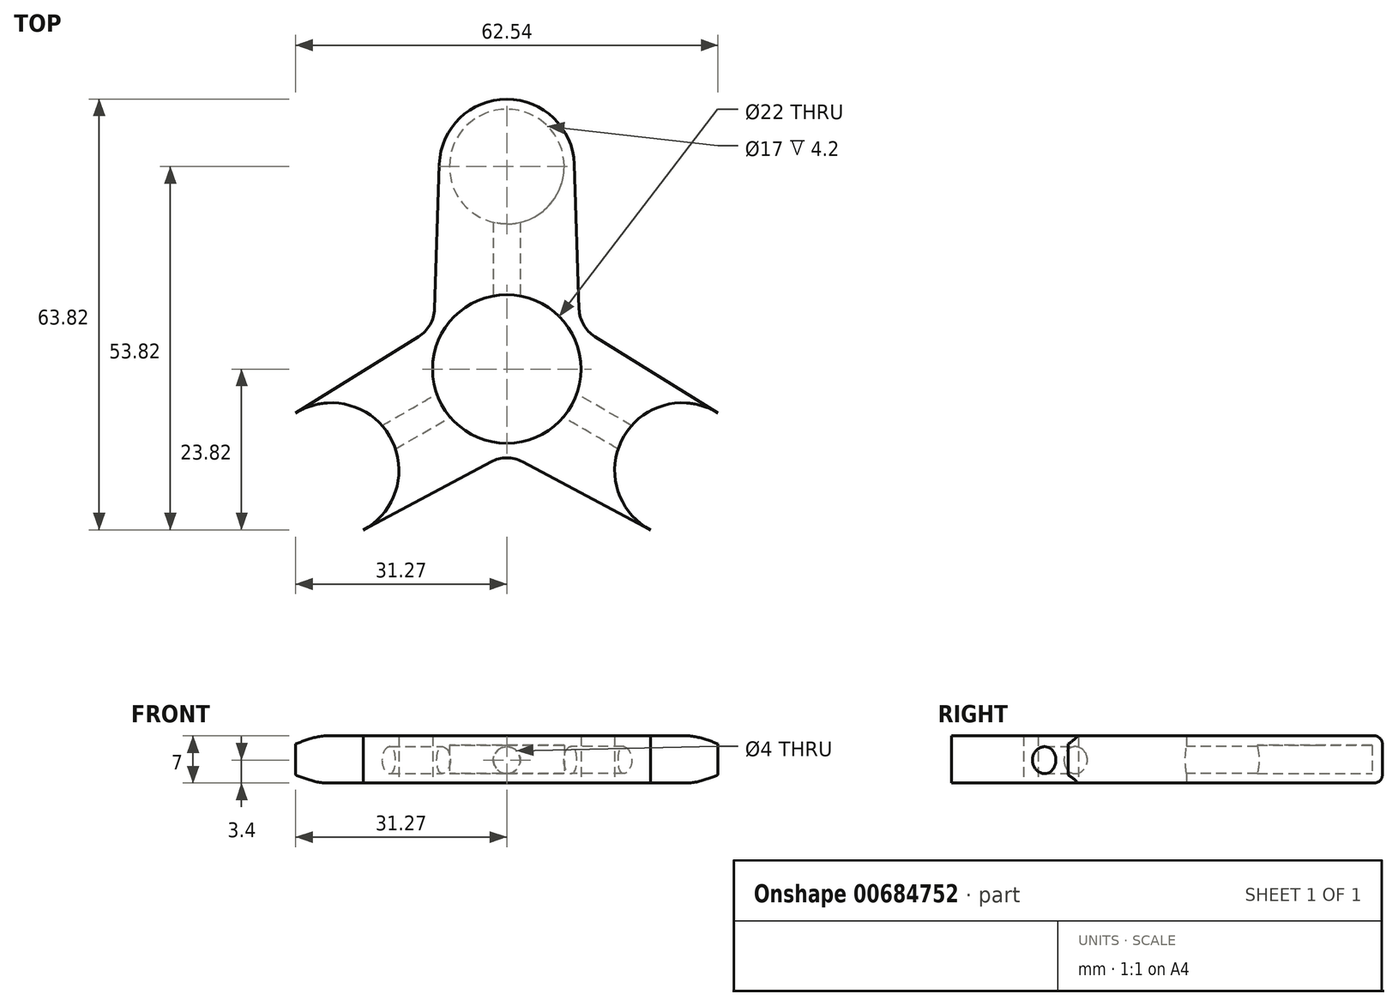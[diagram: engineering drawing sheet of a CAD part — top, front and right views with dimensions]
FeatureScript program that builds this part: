
annotation { "Feature Type Name" : "Feature", "Feature Type Description" : "" }
export const myFeature = defineFeature(function(context is Context, id is Id, definition is map)
    precondition{}
    {
        {
            var Q0;
            Q0=qCreatedBy(makeId("Top.planeOp"),FACE);
            var sketch = newSketch(context, id + "F0", { "sketchPlane" : qUnion([Q0])});
            skCircle(sketch, "E0", {"center": v(0, 0) * mm, "radius": 11 * mm});
            skLineSegment(sketch, "E1", {"start": v(-51.96, 30) * mm, "end": v(51.96, -30) * mm, "construction": true});
            skLineSegment(sketch, "E2.MirrorCS", {"start": v(51.96, 30) * mm, "end": v(-51.96, -30) * mm, "construction": true});
            skCircle(sketch, "E3", {"center": v(0, 30) * mm, "radius": 10 * mm});
            skCircle(sketch, "E4.MirrorC", {"center": v(-25.98, -15) * mm, "radius": 10 * mm});
            skCircle(sketch, "E5.MirrorC", {"center": v(25.98, -15) * mm, "radius": 10 * mm});
            skLineSegment(sketch, "E6", {"start": v(-10, 30.33) * mm, "end": v(-10.7, 8.9) * mm});
            skLineSegment(sketch, "E7", {"start": v(-13.06, 4.82) * mm, "end": v(-31.27, -6.51) * mm});
            skLineSegment(sketch, "E8", {"start": v(10, 30.33) * mm, "end": v(10.7, 8.9) * mm});
            skLineSegment(sketch, "E9.MirrorCS", {"start": v(-21.27, -23.82) * mm, "end": v(-2.35, -13.73) * mm});
            skLineSegment(sketch, "E10.MirrorCS", {"start": v(21.27, -23.82) * mm, "end": v(2.35, -13.73) * mm});
            skLineSegment(sketch, "E11.MirrorCS", {"start": v(31.27, -6.51) * mm, "end": v(13.06, 4.82) * mm});
            skPoint(sketch, "E12.newPointA", {"position": v(-11, 0) * mm});
            skArc(sketch, "E12.filletArc", {"start": v(-13.06, 4.82) * mm, "mid": v(-11.38, 6.57) * mm, "end": v(-10.7, 8.9) * mm});
            skPoint(sketch, "E13.newPointA", {"position": v(5.5, 9.53) * mm});
            skPoint(sketch, "E13.newPointB", {"position": v(11, 0) * mm});
            skArc(sketch, "E13.filletArc", {"start": v(10.7, 8.9) * mm, "mid": v(11.38, 6.57) * mm, "end": v(13.06, 4.82) * mm});
            skPoint(sketch, "E14.newPointA", {"position": v(5.5, -9.53) * mm});
            skPoint(sketch, "E14.newPointB", {"position": v(-5.5, -9.53) * mm});
            skArc(sketch, "E14.filletArc", {"start": v(2.35, -13.73) * mm, "mid": v(0, -13.14) * mm, "end": v(-2.35, -13.73) * mm});
            skLineSegment(sketch, "E15", {"start": v(-8.84, -35.83) * mm, "end": v(22.73, 18.85) * mm, "construction": true});
            skLineSegment(sketch, "E16.MirrorCS", {"start": v(8.84, -35.83) * mm, "end": v(-22.73, 18.85) * mm, "construction": true});
            skSolve(sketch);
        }
        {
            var Q0;
            Q0=makeQuery(id+"F0.imprint","IMPRINT",FACE,{"disambiguationData":[TD([[makeQuery(id+"F0.imprint","IMPRINT",EDGE,{"derivedFrom":sQuery(id+"F0.wireOp",EDGE,"E0")}),-1.0]])]});
            var Q1;
            {var subQ0=sQuery(id+"F0.wireOp",EDGE,"E3");var subQ1=makeQuery(id+"F0.imprint","INTERSECT",VERTEX,{"derivedFrom":[subQ0,sQuery(id+"F0.wireOp",EDGE,"E8")]});Q1=makeQuery(id+"F0.imprint","IMPRINT",FACE,{"disambiguationData":[TD([[makeQuery(id+"F0.imprint","IMPRINT",EDGE,{"disambiguationData":[TD([[subQ1,-1.0]])],"derivedFrom":subQ0}),1.0]])]});}
            var Q2;
            {var subQ0=sQuery(id+"F0.wireOp",EDGE,"E4.MirrorC");var subQ1=makeQuery(id+"F0.imprint","INTERSECT",VERTEX,{"derivedFrom":[subQ0,sQuery(id+"F0.wireOp",EDGE,"E7")]});Q2=makeQuery(id+"F0.imprint","IMPRINT",FACE,{"disambiguationData":[TD([[makeQuery(id+"F0.imprint","IMPRINT",EDGE,{"disambiguationData":[TD([[subQ1,1.0]])],"derivedFrom":subQ0}),-1.0]])]});}
            var Q3;
            {var subQ0=sQuery(id+"F0.wireOp",EDGE,"E5.MirrorC");var subQ1=makeQuery(id+"F0.imprint","INTERSECT",VERTEX,{"derivedFrom":[subQ0,sQuery(id+"F0.wireOp",EDGE,"E11.MirrorCS")]});Q3=makeQuery(id+"F0.imprint","IMPRINT",FACE,{"disambiguationData":[TD([[makeQuery(id+"F0.imprint","IMPRINT",EDGE,{"disambiguationData":[TD([[subQ1,-1.0]])],"derivedFrom":subQ0}),-1.0]])]});}
            var Q4;
            {var subQ5=sQuery(id+"F0.wireOp",EDGE,"lwHCKfIK-zS6e-CTAC-9HsI-oUIeT1y9pyuL");Q4=makeQuery(id+"F0.imprint","IMPRINT",FACE,{"disambiguationData":[TD([[makeQuery(id+"F0.imprint","IMPRINT",EDGE,{"derivedFrom":subQ5}),1.0]])]});}
            var Q5;
            {var subQ1=sQuery(id+"F0.wireOp",EDGE,"E8");Q5=makeQuery(id+"F0.imprint","IMPRINT",FACE,{"disambiguationData":[TD([[makeQuery(id+"F0.imprint","IMPRINT",EDGE,{"derivedFrom":subQ1}),1.0]])]});}
            extrude(context, id + "F1", {"entities" : qUnion([Q0, Q1, Q2, Q3, Q4, Q5]), "depth" : 7 * mm, "offsetDistance" : 25 * mm});
        }
        {
            var Q0;
            Q0=qCreatedBy(makeId("Top.planeOp"),FACE);
            cPlane(context, id + "F2", {"entities" : qUnion([Q0]), "cplaneType" : CPlaneType.OFFSET, "offset" : 1.4 * mm, "width" : 150 * mm, "height" : 150 * mm});
        }
        {
            var Q0;
            Q0=qCreatedBy(id+"F2.planeOp",FACE);
            var sketch = newSketch(context, id + "F3", { "sketchPlane" : qUnion([Q0])});
            skPoint(sketch, "E17.0", {"position": v(0, 30) * mm});
            skPoint(sketch, "E18.0", {"position": v(25.98, -15) * mm});
            skPoint(sketch, "E19.0", {"position": v(-25.98, -15) * mm});
            skCircle(sketch, "E20", {"center": v(25.98, -15) * mm, "radius": 8.5 * mm});
            skCircle(sketch, "E21", {"center": v(-25.98, -15) * mm, "radius": 8.5 * mm});
            skCircle(sketch, "E22", {"center": v(0, 30) * mm, "radius": 8.5 * mm});
            skSolve(sketch);
        }
        {
            var Q0;
            Q0=qSketchRegion(id+"F3",true);
            extrude(context, id + "F4", {"entities" : qUnion([Q0]), "operationType" : NewBodyOperationType.REMOVE, "depth" : 4.2 * mm, "offsetDistance" : 25 * mm});
        }
        {
            var Q0;
            Q0=qCreatedBy(makeId("Front.planeOp"),FACE);
            cPlane(context, id + "F5", {"entities" : qUnion([Q0]), "cplaneType" : CPlaneType.OFFSET, "offset" : 10 * mm, "oppositeDirection" : true, "width" : 150 * mm, "height" : 150 * mm});
        }
        {
            var Q0;
            Q0=qCreatedBy(id+"F5.planeOp",FACE);
            var sketch = newSketch(context, id + "F6", { "sketchPlane" : qUnion([Q0])});
            skCircle(sketch, "E23", {"center": v(0, 3.4) * mm, "radius": 2 * mm});
            skSolve(sketch);
        }
        {
            var Q0;
            Q0=makeQuery(id+"F6.imprint","IMPRINT",FACE,{"disambiguationData":[TD([[makeQuery(id+"F6.imprint","IMPRINT",EDGE,{"derivedFrom":sQuery(id+"F6.wireOp",EDGE,"E23")}),1.0]])]});
            extrude(context, id + "F7", {"entities" : qUnion([Q0]), "operationType" : NewBodyOperationType.REMOVE, "oppositeDirection" : true, "depth" : 12 * mm, "offsetDistance" : 25 * mm});
        }
        {
            var Q0;
            Q0=sQuery(id+"F0.wireOp",EDGE,"E15");
            cPlane(context, id + "F8", {"entities" : qUnion([Q0]), "cplaneType" : CPlaneType.LINE_ANGLE, "offset" : 25 * mm, "angle" : 90 * degree, "width" : 150 * mm, "height" : 150 * mm});
        }
        {
            var Q0;
            Q0=qCreatedBy(id+"F8.planeOp",FACE);
            var sketch = newSketch(context, id + "F9", { "sketchPlane" : qUnion([Q0])});
            skCircle(sketch, "E24", {"center": v(0, 3.4) * mm, "radius": 2 * mm});
            skSolve(sketch);
        }
        {
            var Q0;
            Q0=makeQuery(id+"F9.imprint","IMPRINT",FACE,{"disambiguationData":[TD([[makeQuery(id+"F9.imprint","IMPRINT",EDGE,{"derivedFrom":sQuery(id+"F9.wireOp",EDGE,"E24")}),1.0]])]});
            extrude(context, id + "F10", {"entities" : qUnion([Q0]), "operationType" : NewBodyOperationType.REMOVE, "depth" : 12 * mm, "offsetDistance" : 25 * mm});
        }
        {
            var Q0;
            Q0=sQuery(id+"F0.wireOp",EDGE,"E16.MirrorCS");
            cPlane(context, id + "F11", {"entities" : qUnion([Q0]), "cplaneType" : CPlaneType.LINE_ANGLE, "offset" : 25 * mm, "angle" : 90 * degree, "width" : 150 * mm, "height" : 150 * mm});
        }
        {
            var Q0;
            Q0=qCreatedBy(id+"F11.planeOp",FACE);
            var sketch = newSketch(context, id + "F12", { "sketchPlane" : qUnion([Q0])});
            skCircle(sketch, "E25", {"center": v(0, 3.4) * mm, "radius": 2 * mm});
            skSolve(sketch);
        }
        {
            var Q0;
            Q0=makeQuery(id+"F12.imprint","IMPRINT",FACE,{"disambiguationData":[TD([[makeQuery(id+"F12.imprint","IMPRINT",EDGE,{"derivedFrom":sQuery(id+"F12.wireOp",EDGE,"E25")}),1.0]])]});
            extrude(context, id + "F13", {"entities" : qUnion([Q0]), "operationType" : NewBodyOperationType.REMOVE, "oppositeDirection" : true, "depth" : 12 * mm, "offsetDistance" : 25 * mm});
        }
        {
            var Q0;
            Q0=makeQuery(id+"F1.opExtrude","CAP_EDGE",EDGE,{"disambiguationData":[OSD([sQuery(id+"F0.wireOp",EDGE,"E3")])],"isStart":false});
            var Q1;
            Q1=makeQuery(id+"F1.opExtrude","CAP_EDGE",EDGE,{"disambiguationData":[OSD([sQuery(id+"F0.wireOp",EDGE,"E3")])],"isStart":true});
            fillet(context, id + "F14", {"entities" : qUnion([Q0, Q1]), "radius" : 1.2 * mm, "tangentPropagation" : true, "allowEdgeOverflow" : false});
        }
    });
